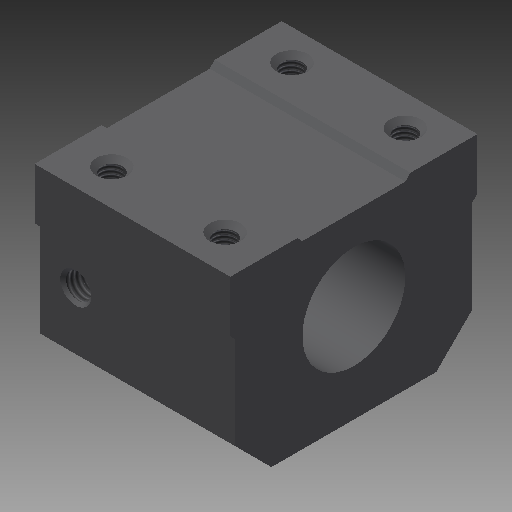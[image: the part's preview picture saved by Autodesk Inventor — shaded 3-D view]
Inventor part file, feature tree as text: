
AUTODESK INVENTOR PART (.ipt)
format: ipt  version: 2018 (Build 220112000, 112)  size: 211,456 bytes
history: native  units: mm
features: sketch x11, other x7, extrude x5, revolve x2, hole x2, pattern_linear x1
ambient origin geometry x8: Origin, YZ Plane, XZ Plane, XY Plane, X Axis, Y Axis, Z Axis, Center Point
bodies: Solid1 (feature_tree)
feature tree (28):
  extrude  "Extrusion1"  Depth=38.0mm TaperAngle=0.0deg
  extrude  "Extrusion2"  TaperAngle=360.0deg  [1 undecoded]
  extrude  "Extrusion3"  Depth=0.8mm TaperAngle=0.0deg
  revolve  "Revolution1"  [1 undecoded]
  revolve  "Revolution2"  [1 undecoded]
  extrude  "Extrusion4"  Depth=24.546069mm
  extrude  "Extrusion5"  Depth=24.546069mm
  hole  "Hole1"  [1 undecoded]
  hole  "Hole2"  [1 undecoded]
  pattern_linear  "Rectangular Pattern1"  Spacing1=1.0mm  [1 undecoded]
  other  "bnt_nut_1_XY"
  other  "bnt_nut_1_YZ"
  other  "bnt_nut_1_ZX"
  other  "bnt_nut_1_X"
  other  "bnt_nut_1_Y"
  other  "bnt_nut_1_Z"
  other  "bnt_nut_1_Center"
  sketch  "Sketch10"  dims[d38=1.15mm d39=20.0mm]
  sketch  "Sketch11"  dims[d41=46.0mm d43=23.0mm d45=1.0mm d46=48.0mm d47=1.0mm d48=36.0mm d49=10.0mm d50=10.0mm d51=20.0mm d52=13.0mm d53=13.0mm d54=32.0mm d55=16.0mm d56=135.0deg d57=18.0mm d58=18.0mm d59=8.0mm d60=6.0mm d61=7.0mm d62=31.0mm]
  sketch  "Sketch_1"  dims[d0=38.0mm d1=0.0mm d2=58.0mm d3=0.0mm]
  sketch  "Sketch_2"  dims[d4=4.6mm d5=0.0mm d6=360.0deg]
  sketch  "Sketch_3"  dims[d7=360.0deg d8=0.8mm d9=0.0mm]
  sketch  "Sketch_4"  dims[d10=0.8mm d11=0.0mm]
  sketch  "Sketch_5"  dims[d12=4.917mm d13=10.5415mm d14=6.0mm d15=2.0mm d16=90.0deg d17=14.140584mm d18=120.0deg]
  sketch  "Sketch_6"  dims[d19=4.134mm d20=10.0mm d21=6.0mm d22=2.0mm d23=90.0deg d24=13.0mm d25=120.0deg d26=20.0mm d28=22.0mm d29=20.0mm d31=35.0mm]
  sketch  "Sketch_7"  dims[d32=0.0mm d33=58.0mm]
  sketch  "Sketch8"  dims[d34=1.15mm d35=24.546069mm]
  sketch  "Sketch9"  dims[d36=4.6mm d37=24.546069mm]
note: 6 required parameter values undecoded (feature->parameter linkage not recoverable at this tier; creation-order binding heuristic only, values carry confidence <= 0.55)